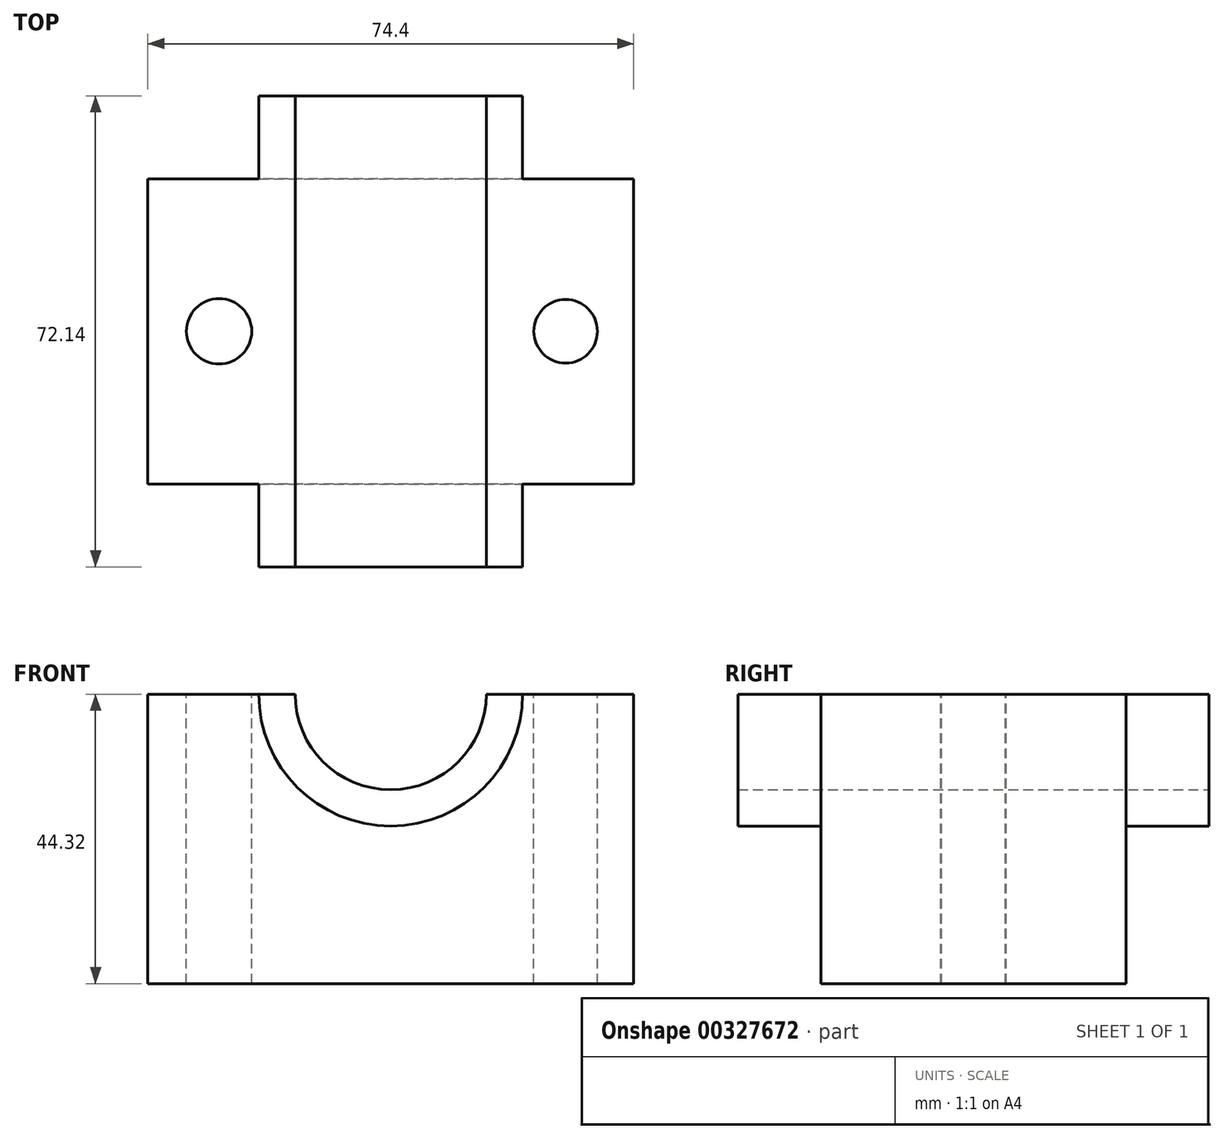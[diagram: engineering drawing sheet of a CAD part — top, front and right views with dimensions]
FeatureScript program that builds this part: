
annotation { "Feature Type Name" : "Feature", "Feature Type Description" : "" }
export const myFeature = defineFeature(function(context is Context, id is Id, definition is map)
    precondition{}
    {
        {
            var Q0;
            Q0=qCreatedBy(makeId("Front.planeOp"),FACE);
            var sketch = newSketch(context, id + "F0", { "sketchPlane" : qUnion([Q0])});
            skLineSegment(sketch, "E0.bottom", {"start": v(37.2, -22.16) * mm, "end": v(-37.2, -22.16) * mm});
            skLineSegment(sketch, "E0.top", {"start": v(37.2, 22.16) * mm, "end": v(-37.2, 22.16) * mm});
            skLineSegment(sketch, "E0.left", {"start": v(37.2, -22.16) * mm, "end": v(37.2, 22.16) * mm});
            skLineSegment(sketch, "E0.right", {"start": v(-37.2, -22.16) * mm, "end": v(-37.2, 22.16) * mm});
            skPoint(sketch, "E0.middle", {"position": v(0, 0) * mm});
            skArc(sketch, "E1", {"start": v(-20.2, 22.16) * mm, "mid": v(0, 1.96) * mm, "end": v(20.2, 22.16) * mm});
            skArc(sketch, "E2", {"start": v(-14.64, 22.16) * mm, "mid": v(0, 7.52) * mm, "end": v(14.64, 22.16) * mm});
            skSolve(sketch);
        }
        {
            var Q0;
            Q0=makeQuery(id+"F0.imprint","IMPRINT",FACE,{"disambiguationData":[TD([[makeQuery(id+"F0.imprint","IMPRINT",EDGE,{"derivedFrom":sQuery(id+"F0.wireOp",EDGE,"E0.bottom")}),-1.0]])]});
            extrude(context, id + "F1", {"entities" : qUnion([Q0]), "endBound" : BoundingType.SYMMETRIC, "depth" : 46.74 * mm});
        }
        {
            var Q0;
            {var subQ0=sQuery(id+"F0.wireOp",EDGE,"E1");Q0=makeQuery(id+"F0.imprint","IMPRINT",FACE,{"disambiguationData":[TD([[makeQuery(id+"F0.imprint","IMPRINT",EDGE,{"derivedFrom":subQ0}),1.0]])]});}
            extrude(context, id + "F2", {"entities" : qUnion([Q0]), "operationType" : NewBodyOperationType.ADD, "endBound" : BoundingType.SYMMETRIC, "depth" : 72.14 * mm});
        }
        {
            var Q0;
            {var subQ0=sQuery(id+"F0.wireOp",EDGE,"E0.top");var subQ1=makeQuery(id+"F0.imprint","INTERSECT",VERTEX,{"disambiguationData":[OD(1.0)],"derivedFrom":[subQ0,sQuery(id+"F0.wireOp",EDGE,"E1")]});Q0=makeQuery(id+"F2.boolean.opBoolean","MERGE",FACE,{"derivedFrom":[makeQuery(id+"F1.opExtrude","SWEPT_FACE",FACE,{"disambiguationData":[OSD([subQ0]),TDD([makeQuery(id+"F0.imprint","IMPRINT",EDGE,{"disambiguationData":[TD([[makeQuery(id+"F0.imprint","INTERSECT",VERTEX,{"derivedFrom":[subQ0,sQuery(id+"F0.wireOp",EDGE,"E0.left")]}),-1.0]])],"derivedFrom":subQ0})])]}),makeQuery(id+"F2.opExtrude","SWEPT_FACE",FACE,{"disambiguationData":[OSD([subQ0]),TDD([makeQuery(id+"F0.imprint","IMPRINT",EDGE,{"disambiguationData":[TD([[subQ1,-1.0]])],"derivedFrom":subQ0})])]})]});}
            var sketch = newSketch(context, id + "F3", { "sketchPlane" : qUnion([Q0])});
            skCircle(sketch, "E3", {"center": v(-26.3, 0) * mm, "radius": 5 * mm});
            skCircle(sketch, "E4", {"center": v(26.8, 0) * mm, "radius": 4.87 * mm});
            skSolve(sketch);
        }
        {
            var Q0;
            Q0 = qSketchRegion(id + "F3", true);
            extrude(context, id + "F4", {"entities" : qUnion([Q0]), "operationType" : NewBodyOperationType.REMOVE, "oppositeDirection" : true, "depth" : 64 * mm});
        }
    });
